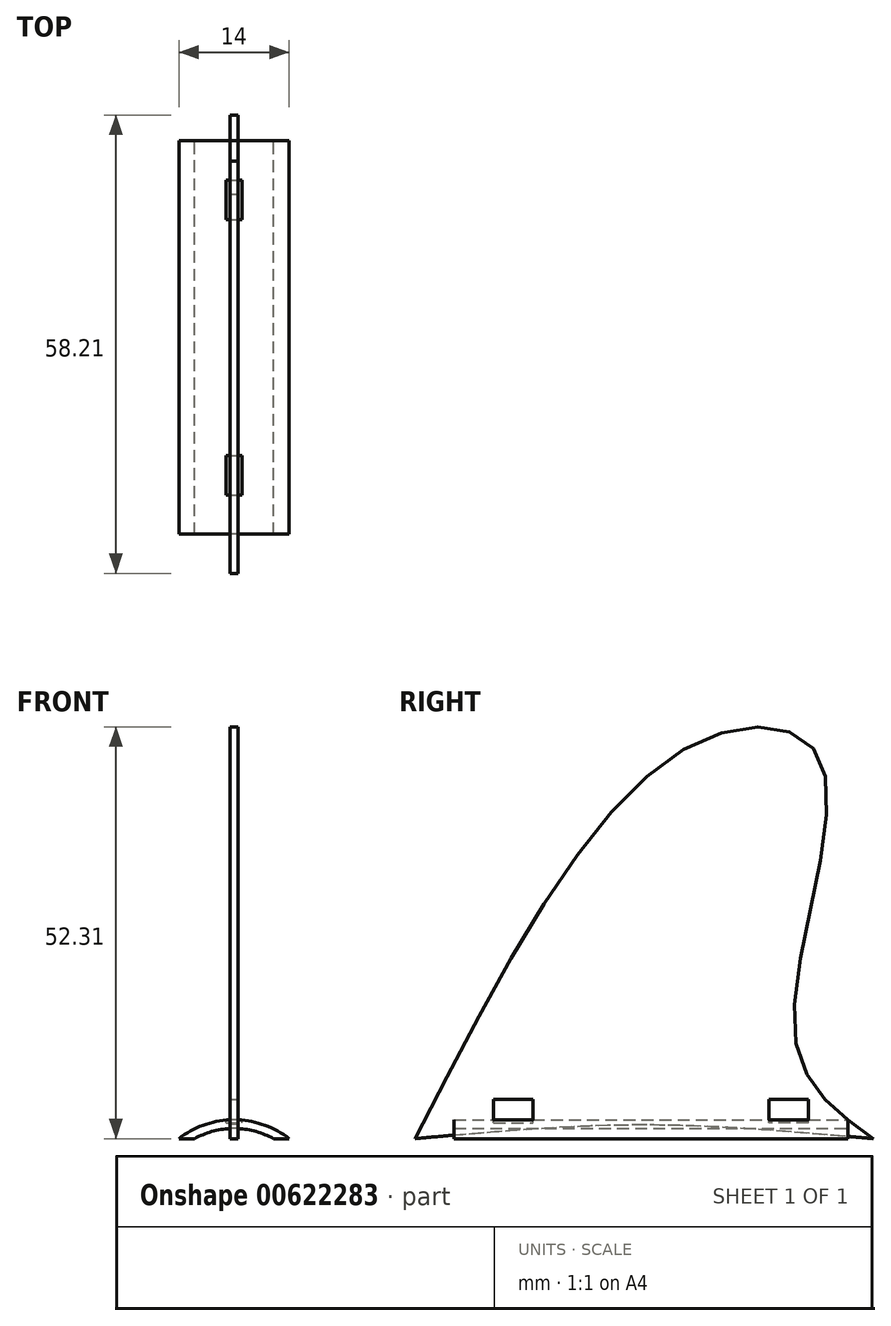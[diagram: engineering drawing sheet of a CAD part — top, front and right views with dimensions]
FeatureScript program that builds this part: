
annotation { "Feature Type Name" : "Feature", "Feature Type Description" : "" }
export const myFeature = defineFeature(function(context is Context, id is Id, definition is map)
    precondition{}
    {
        {
            var Q0;
            Q0=qCreatedBy(makeId("Front.planeOp"),FACE);
            var sketch = newSketch(context, id + "F0", { "sketchPlane" : qUnion([Q0])});
            skArc(sketch, "E0", {"start": v(5, 0) * mm, "mid": v(0, 1.3) * mm, "end": v(-5, 0) * mm});
            skArc(sketch, "E1", {"start": v(7, 0) * mm, "mid": v(0, 2.4) * mm, "end": v(-7, 0) * mm});
            skLineSegment(sketch, "E2", {"start": v(-7, 0) * mm, "end": v(-5, 0) * mm});
            skLineSegment(sketch, "E3", {"start": v(5, 0) * mm, "end": v(7, 0) * mm});
            skSolve(sketch);
        }
        {
            var Q0;
            Q0=qCreatedBy(makeId("Right.planeOp"),FACE);
            var sketch = newSketch(context, id + "F1", { "sketchPlane" : qUnion([Q0])});
            skFitSpline(sketch, "E4", {"points": [v(28.24, 0) * mm, v(18.21, 13.59) * mm, v(21.58, 48.01) * mm, v(5.2, 50) * mm, v(-29.97, 0) * mm], "startDerivative": vector(-75.1, 53.38) * mm, "endDerivative": vector(-92.7, -181.14) * mm});
            skFitSpline(sketch, "E5", {"points": [v(-29.97, 0) * mm, v(-0.9, 1.8) * mm, v(28.24, 0) * mm], "startDerivative": vector(58.15, 5.4) * mm, "endDerivative": vector(58.26, -5.39) * mm});
            skSolve(sketch);
        }
        {
            var Q0;
            Q0 = qSketchRegion(id + "F0", true);
            extrude(context, id + "F2", {"entities" : qUnion([Q0]), "endBound" : BoundingType.SYMMETRIC, "depth" : 50 * mm, "offsetDistance" : 25 * mm});
        }
        {
            var Q0;
            Q0 = qSketchRegion(id + "F1", true);
            extrude(context, id + "F3", {"entities" : qUnion([Q0]), "endBound" : BoundingType.SYMMETRIC, "depth" : 1 * mm, "offsetDistance" : 25 * mm});
        }
        {
            var Q0;
            Q0=qCreatedBy(makeId("Right.planeOp"),FACE);
            var sketch = newSketch(context, id + "F4", { "sketchPlane" : qUnion([Q0])});
            skLineSegment(sketch, "E6.bottom", {"start": v(-20, 2) * mm, "end": v(-15, 2) * mm});
            skLineSegment(sketch, "E6.top", {"start": v(-20, 5) * mm, "end": v(-15, 5) * mm});
            skLineSegment(sketch, "E6.left", {"start": v(-20, 2) * mm, "end": v(-20, 5) * mm});
            skLineSegment(sketch, "E6.right", {"start": v(-15, 2) * mm, "end": v(-15, 5) * mm});
            skLineSegment(sketch, "E7.MirrorCS", {"start": v(20, 5) * mm, "end": v(15, 5) * mm});
            skLineSegment(sketch, "E8.MirrorCS", {"start": v(20, 2) * mm, "end": v(20, 5) * mm});
            skLineSegment(sketch, "E9.MirrorCS", {"start": v(15, 2) * mm, "end": v(15, 5) * mm});
            skLineSegment(sketch, "E10.MirrorCS", {"start": v(20, 2) * mm, "end": v(15, 2) * mm});
            skSolve(sketch);
        }
        {
            var Q0;
            Q0 = qSketchRegion(id + "F4", true);
            extrude(context, id + "F5", {"entities" : qUnion([Q0]), "operationType" : NewBodyOperationType.REMOVE, "endBound" : BoundingType.SYMMETRIC, "oppositeDirection" : true, "depth" : 2 * mm, "offsetDistance" : 25 * mm});
        }
    });
